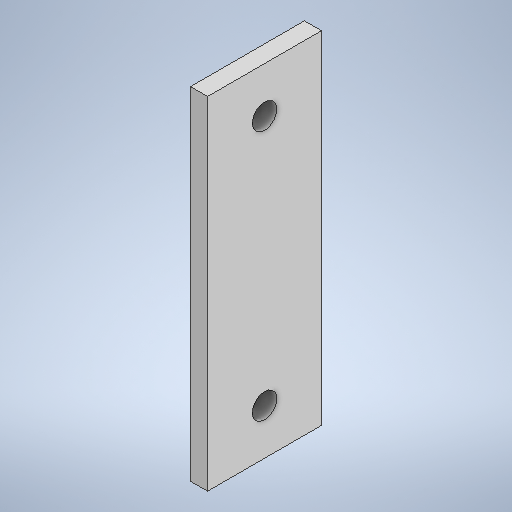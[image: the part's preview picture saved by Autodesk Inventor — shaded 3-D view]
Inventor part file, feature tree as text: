
AUTODESK INVENTOR PART (.ipt)
format: ipt  version: 2025.2 (Build 292293000, 293)  size: 223,232 bytes
history: native  units: mm
features: extrude x1, sketch x1
ambient origin geometry x8: Origin, YZ Plane, XZ Plane, XY Plane, X Axis, Y Axis, Z Axis, Center Point
bodies: Solid1 (feature_tree)
feature tree (2):
  extrude  "Extrusion1"  Depth=20.0mm
  sketch  "Sketch1"  dims[d0=60.0mm d1=20.0mm d2=8.0mm d3=8.0mm d4=4.3mm d5=4.3mm d6=3.0mm d7=0.0mm]
